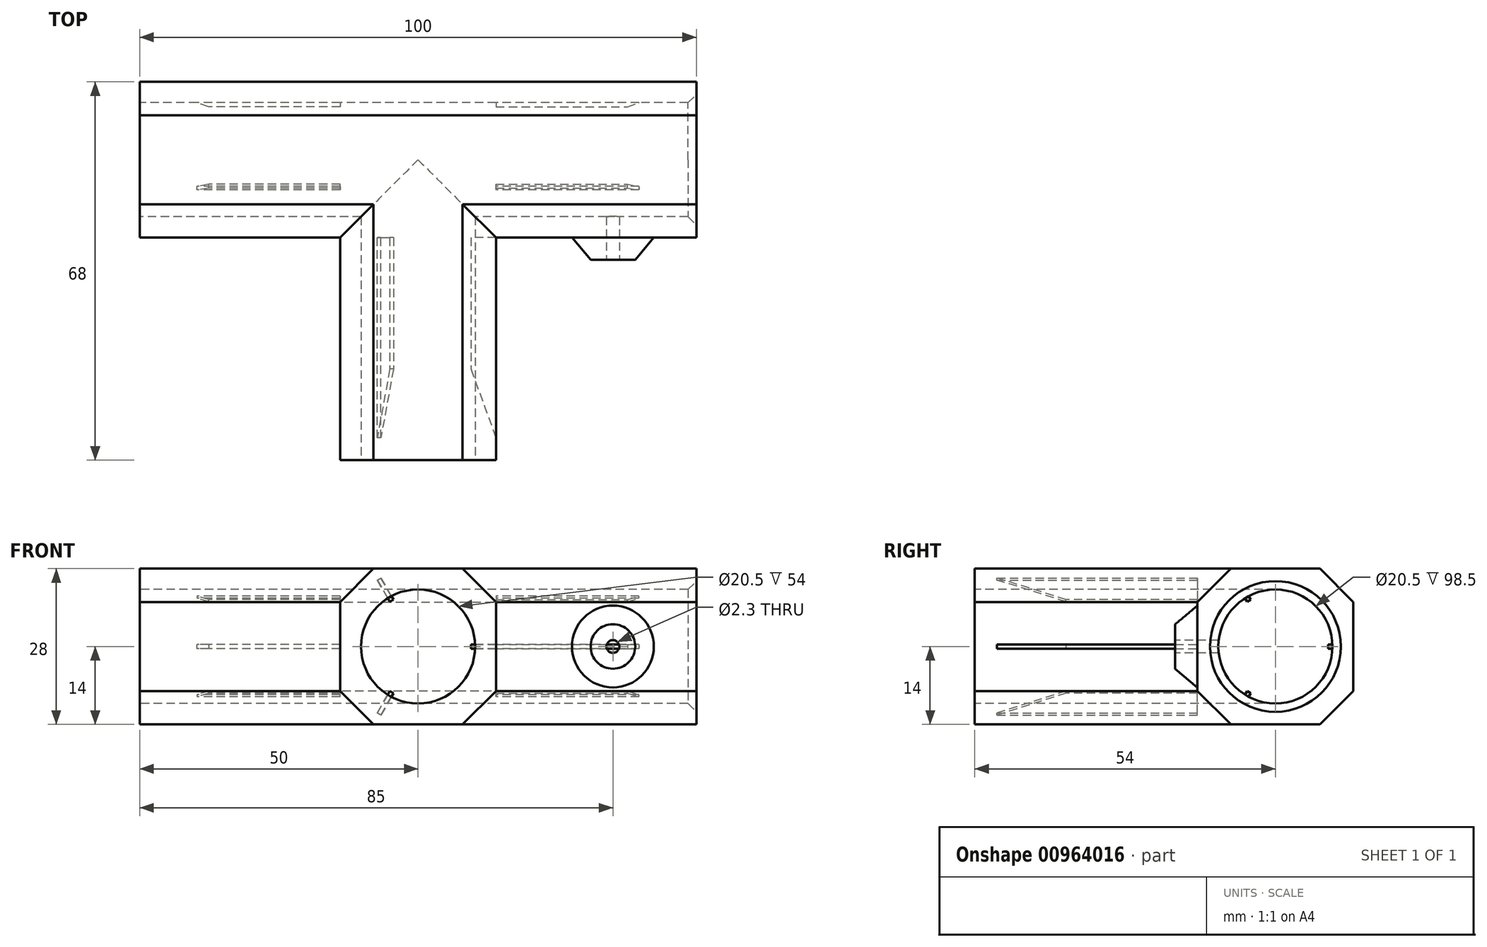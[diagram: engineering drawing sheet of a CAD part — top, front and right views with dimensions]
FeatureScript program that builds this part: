
annotation { "Feature Type Name" : "Feature", "Feature Type Description" : "" }
export const myFeature = defineFeature(function(context is Context, id is Id, definition is map)
    precondition{}
    {
        {
            var Q0;
            Q0=qCreatedBy(makeId("Top.planeOp"),FACE);
            var sketch = newSketch(context, id + "F0", { "sketchPlane" : qUnion([Q0])});
            skCircle(sketch, "E0", {"center": v(0, 0) * mm, "radius": 50 * mm, "construction": true});
            skLineSegment(sketch, "E1", {"start": v(-50, 0) * mm, "end": v(50, 0) * mm, "construction": true});
            skLineSegment(sketch, "E2", {"start": v(0, 50) * mm, "end": v(0, -50) * mm, "construction": true});
            skSolve(sketch);
        }
        {
            var Q0;
            Q0=qCreatedBy(makeId("Top.planeOp"),FACE);
            var sketch = newSketch(context, id + "F1", { "sketchPlane" : qUnion([Q0])});
            skLineSegment(sketch, "E3.bottom", {"start": v(-50, 14) * mm, "end": v(50, 14) * mm});
            skLineSegment(sketch, "E3.top", {"start": v(-50, -14) * mm, "end": v(-14, -14) * mm});
            skLineSegment(sketch, "E3.left", {"start": v(-50, 14) * mm, "end": v(-50, -14) * mm});
            skLineSegment(sketch, "E3.right", {"start": v(50, 14) * mm, "end": v(50, -14) * mm});
            skLineSegment(sketch, "E4.bottom", {"start": v(14, -54) * mm, "end": v(-14, -54) * mm});
            skLineSegment(sketch, "E4.left", {"start": v(14, -54) * mm, "end": v(14, -14) * mm});
            skLineSegment(sketch, "E4.right", {"start": v(-14, -54) * mm, "end": v(-14, -14) * mm});
            skLineSegment(sketch, "E5.trimOffspring", {"start": v(14, -14) * mm, "end": v(50, -14) * mm});
            skLineSegment(sketch, "E6", {"start": v(35, 0) * mm, "end": v(35, -18) * mm, "construction": true});
            skLineSegment(sketch, "E7", {"start": v(42.36, -14) * mm, "end": v(39, -18) * mm});
            skLineSegment(sketch, "E8", {"start": v(39, -18) * mm, "end": v(31, -18) * mm});
            skLineSegment(sketch, "E9.MirrorCS", {"start": v(27.64, -14) * mm, "end": v(31, -18) * mm});
            skLineSegment(sketch, "E10", {"start": v(35, -18) * mm, "end": v(35, -14) * mm});
            skSolve(sketch);
        }
        {
            var Q0;
            Q0=makeQuery(id+"F1.imprint","IMPRINT",FACE,{"disambiguationData":[TD([[makeQuery(id+"F1.imprint","IMPRINT",EDGE,{"derivedFrom":sQuery(id+"F1.wireOp",EDGE,"E3.bottom")}),-1.0]])]});
            extrude(context, id + "F2", {"entities" : qUnion([Q0]), "depth" : 28 * mm, "offsetDistance" : 25 * mm, "symmetric" : true});
        }
        {
            var Q0;
            Q0=makeQuery(id+"F2.opExtrude","SWEPT_FACE",FACE,{"disambiguationData":[OSD([sQuery(id+"F1.wireOp",EDGE,"E3.left")])]});
            var sketch = newSketch(context, id + "F3", { "sketchPlane" : qUnion([Q0])});
            skCircle(sketch, "E11", {"center": v(0, 0) * mm, "radius": 10.25 * mm});
            skSolve(sketch);
        }
        {
            var Q0;
            Q0 = qSketchRegion(id + "F3", true);
            extrude(context, id + "F4", {"entities" : qUnion([Q0]), "operationType" : NewBodyOperationType.REMOVE, "endBound" : BoundingType.THROUGH_ALL, "oppositeDirection" : true, "depth" : 25 * mm, "offsetDistance" : 25 * mm});
        }
        {
            var Q0;
            Q0=makeQuery(id+"F2.opExtrude","SWEPT_FACE",FACE,{"disambiguationData":[OSD([sQuery(id+"F1.wireOp",EDGE,"E4.bottom")])]});
            var sketch = newSketch(context, id + "F5", { "sketchPlane" : qUnion([Q0])});
            skCircle(sketch, "E12", {"center": v(0, 0) * mm, "radius": 10.25 * mm});
            skSolve(sketch);
        }
        {
            var Q0;
            Q0 = qSketchRegion(id + "F5", true);
            extrude(context, id + "F6", {"entities" : qUnion([Q0]), "operationType" : NewBodyOperationType.REMOVE, "endBound" : BoundingType.UP_TO_NEXT, "oppositeDirection" : true, "depth" : 25 * mm, "offsetDistance" : 25 * mm});
        }
        {
            var Q0;
            {var subQ0=sQuery(id+"F1.wireOp",EDGE,"E7");Q0=makeQuery(id+"F1.imprint","IMPRINT",FACE,{"disambiguationData":[TD([[makeQuery(id+"F1.imprint","IMPRINT",EDGE,{"derivedFrom":subQ0}),-1.0]])]});}
            var Q1;
            Q1=sQuery(id+"F1.wireOp",EDGE,"E10");
            revolve(context, id + "F7", {"operationType" : NewBodyOperationType.ADD, "surfaceOperationType" : NewSurfaceOperationType.NEW, "entities" : qUnion([Q0]), "axis" : qUnion([Q1]), "revolveType" : RevolveType.FULL});
        }
        {
            var Q0;
            Q0=makeQuery(id+"F7.opRevolve","SWEPT_FACE",FACE,{"disambiguationData":[OSD([sQuery(id+"F1.wireOp",EDGE,"E8")])]});
            var sketch = newSketch(context, id + "F8", { "sketchPlane" : qUnion([Q0])});
            skCircle(sketch, "E13", {"center": v(35, 0) * mm, "radius": 1.15 * mm});
            skSolve(sketch);
        }
        {
            var Q0;
            Q0 = qSketchRegion(id + "F8", true);
            extrude(context, id + "F9", {"entities" : qUnion([Q0]), "operationType" : NewBodyOperationType.REMOVE, "endBound" : BoundingType.UP_TO_NEXT, "oppositeDirection" : true, "depth" : 25 * mm, "offsetDistance" : 25 * mm});
        }
        {
            var Q0;
            Q0=makeQuery(id+"F2.opExtrude","CAP_EDGE",EDGE,{"disambiguationData":[OSD([sQuery(id+"F1.wireOp",EDGE,"E3.bottom")])],"isStart":true});
            var Q1;
            Q1=makeQuery(id+"F2.opExtrude","CAP_EDGE",EDGE,{"disambiguationData":[OSD([sQuery(id+"F1.wireOp",EDGE,"E3.bottom")])],"isStart":false});
            var Q2;
            Q2=makeQuery(id+"F2.opExtrude","CAP_EDGE",EDGE,{"disambiguationData":[OSD([sQuery(id+"F1.wireOp",EDGE,"E3.top")])],"isStart":true});
            var Q3;
            Q3=makeQuery(id+"F2.opExtrude","CAP_EDGE",EDGE,{"disambiguationData":[OSD([sQuery(id+"F1.wireOp",EDGE,"E5.trimOffspring")])],"isStart":true});
            var Q4;
            Q4=makeQuery(id+"F2.opExtrude","CAP_EDGE",EDGE,{"disambiguationData":[OSD([sQuery(id+"F1.wireOp",EDGE,"E4.left")])],"isStart":true});
            var Q5;
            Q5=makeQuery(id+"F2.opExtrude","CAP_EDGE",EDGE,{"disambiguationData":[OSD([sQuery(id+"F1.wireOp",EDGE,"E4.right")])],"isStart":true});
            var Q6;
            Q6=makeQuery(id+"F2.opExtrude","CAP_EDGE",EDGE,{"disambiguationData":[OSD([sQuery(id+"F1.wireOp",EDGE,"E4.right")])],"isStart":false});
            var Q7;
            Q7=makeQuery(id+"F2.opExtrude","CAP_EDGE",EDGE,{"disambiguationData":[OSD([sQuery(id+"F1.wireOp",EDGE,"E3.top")])],"isStart":false});
            var Q8;
            Q8=makeQuery(id+"F2.opExtrude","CAP_EDGE",EDGE,{"disambiguationData":[OSD([sQuery(id+"F1.wireOp",EDGE,"E5.trimOffspring")])],"isStart":false});
            var Q9;
            Q9=makeQuery(id+"F2.opExtrude","CAP_EDGE",EDGE,{"disambiguationData":[OSD([sQuery(id+"F1.wireOp",EDGE,"E4.left")])],"isStart":false});
            chamfer(context, id + "F10", {"entities" : qUnion([Q0, Q1, Q2, Q3, Q4, Q5, Q6, Q7, Q8, Q9]), "width" : 6 * mm, "tangentPropagation" : true});
        }
        {
            var Q0;
            Q0=makeQuery(id+"F4.boolean.opBoolean","COPY",EDGE,{"derivedFrom":makeQuery(id+"F4.opExtrude","CAP_EDGE",EDGE,{"disambiguationData":[OSD([sQuery(id+"F3.wireOp",EDGE,"E11")])],"isStart":true})});
            var Q1;
            Q1=makeQuery(id+"F6.boolean.opBoolean","COPY",EDGE,{"derivedFrom":makeQuery(id+"F6.opExtrude","CAP_EDGE",EDGE,{"disambiguationData":[OSD([sQuery(id+"F5.wireOp",EDGE,"E12")])],"isStart":true})});
            var Q2;
            Q2=makeQuery(id+"F4.boolean.opBoolean","INTERSECT",EDGE,{"derivedFrom":[makeQuery(id+"F2.opExtrude","SWEPT_FACE",FACE,{"disambiguationData":[OSD([sQuery(id+"F1.wireOp",EDGE,"E3.right")])]}),makeQuery(id+"F4.opExtrude","SWEPT_FACE",FACE,{"disambiguationData":[OSD([sQuery(id+"F3.wireOp",EDGE,"E11")])]})]});
            chamfer(context, id + "F11", {"entities" : qUnion([Q0, Q1, Q2]), "width" : 1.5 * mm, "tangentPropagation" : true});
        }
        {
            var Q0;
            Q0=qCreatedBy(makeId("Top.planeOp"),FACE);
            var sketch = newSketch(context, id + "F12", { "sketchPlane" : qUnion([Q0])});
            skLineSegment(sketch, "E14", {"start": v(0, 0) * mm, "end": v(50, 0) * mm, "construction": true});
            skLineSegment(sketch, "E15", {"start": v(14, 14) * mm, "end": v(14, 9.5) * mm});
            skLineSegment(sketch, "E16", {"start": v(14, 9.5) * mm, "end": v(37.64, 9.5) * mm});
            skLineSegment(sketch, "E17", {"start": v(37.64, 9.5) * mm, "end": v(50, 14) * mm});
            skLineSegment(sketch, "E18", {"start": v(50, 14) * mm, "end": v(14, 14) * mm});
            skSolve(sketch);
        }
        {
            var Q0;
            Q0 = qSketchRegion(id + "F12", true);
            extrude(context, id + "F13", {"entities" : qUnion([Q0]), "depth" : 0.75 * mm, "offsetDistance" : 25 * mm, "symmetric" : true});
        }
        {
            var Q0;
            Q0=makeQuery(id+"F13.opExtrude","SWEPT_BODY",BODY,{"disambiguationData":[OSD([sQuery(id+"F12.wireOp",EDGE,"E15"),sQuery(id+"F12.wireOp",EDGE,"E16"),sQuery(id+"F12.wireOp",EDGE,"E17"),sQuery(id+"F12.wireOp",EDGE,"E18")])]});
            var Q1;
            Q1=sQuery(id+"F0.wireOp",EDGE,"E1");
            circularPattern(context, id + "F14", {"entities" : qUnion([Q0]), "axis" : qUnion([Q1]), "angle" : 360 * degree, "instanceCount" : 3, "equalSpace" : true});
        }
        {
            var Q0;
            Q0=makeQuery(id+"F14.opPattern","COPY",BODY,{"derivedFrom":makeQuery(id+"F13.opExtrude","SWEPT_BODY",BODY,{"disambiguationData":[OSD([sQuery(id+"F12.wireOp",EDGE,"E15"),sQuery(id+"F12.wireOp",EDGE,"E16"),sQuery(id+"F12.wireOp",EDGE,"E17"),sQuery(id+"F12.wireOp",EDGE,"E18")])]}),"instanceName":"1"});
            var Q1;
            Q1=makeQuery(id+"F14.opPattern","COPY",BODY,{"derivedFrom":makeQuery(id+"F13.opExtrude","SWEPT_BODY",BODY,{"disambiguationData":[OSD([sQuery(id+"F12.wireOp",EDGE,"E15"),sQuery(id+"F12.wireOp",EDGE,"E16"),sQuery(id+"F12.wireOp",EDGE,"E17"),sQuery(id+"F12.wireOp",EDGE,"E18")])]}),"instanceName":"2"});
            var Q2;
            Q2=makeQuery(id+"F14.opPattern","COPY",BODY,{"derivedFrom":makeQuery(id+"F13.opExtrude","SWEPT_BODY",BODY,{"disambiguationData":[OSD([sQuery(id+"F12.wireOp",EDGE,"E15"),sQuery(id+"F12.wireOp",EDGE,"E16"),sQuery(id+"F12.wireOp",EDGE,"E17"),sQuery(id+"F12.wireOp",EDGE,"E18")])]}),"instanceName":"3"});
            var Q3;
            Q3=makeQuery(id+"F14.opPattern","COPY",BODY,{"derivedFrom":makeQuery(id+"F13.opExtrude","SWEPT_BODY",BODY,{"disambiguationData":[OSD([sQuery(id+"F12.wireOp",EDGE,"E15"),sQuery(id+"F12.wireOp",EDGE,"E16"),sQuery(id+"F12.wireOp",EDGE,"E17"),sQuery(id+"F12.wireOp",EDGE,"E18")])]}),"instanceName":"4"});
            var Q4;
            Q4=makeQuery(id+"F13.opExtrude","SWEPT_BODY",BODY,{"disambiguationData":[OSD([sQuery(id+"F12.wireOp",EDGE,"E15"),sQuery(id+"F12.wireOp",EDGE,"E16"),sQuery(id+"F12.wireOp",EDGE,"E17"),sQuery(id+"F12.wireOp",EDGE,"E18")])]});
            var Q5;
            Q5=sQuery(id+"F0.wireOp",EDGE,"E0");
            circularPattern(context, id + "F15", {"entities" : qUnion([Q0, Q1, Q2, Q3, Q4]), "axis" : qUnion([Q5]), "angle" : 90 * degree, "instanceCount" : 2, "oppositeDirection" : true, "equalSpace" : true});
        }
        {
            var Q0;
            Q0=makeQuery(id+"F13.opExtrude","SWEPT_BODY",BODY,{"disambiguationData":[OSD([sQuery(id+"F12.wireOp",EDGE,"E15"),sQuery(id+"F12.wireOp",EDGE,"E16"),sQuery(id+"F12.wireOp",EDGE,"E17"),sQuery(id+"F12.wireOp",EDGE,"E18")])]});
            var Q1;
            Q1=makeQuery(id+"F14.opPattern","COPY",BODY,{"derivedFrom":makeQuery(id+"F13.opExtrude","SWEPT_BODY",BODY,{"disambiguationData":[OSD([sQuery(id+"F12.wireOp",EDGE,"E15"),sQuery(id+"F12.wireOp",EDGE,"E16"),sQuery(id+"F12.wireOp",EDGE,"E17"),sQuery(id+"F12.wireOp",EDGE,"E18")])]}),"instanceName":"4"});
            var Q2;
            Q2=makeQuery(id+"F14.opPattern","COPY",BODY,{"derivedFrom":makeQuery(id+"F13.opExtrude","SWEPT_BODY",BODY,{"disambiguationData":[OSD([sQuery(id+"F12.wireOp",EDGE,"E15"),sQuery(id+"F12.wireOp",EDGE,"E16"),sQuery(id+"F12.wireOp",EDGE,"E17"),sQuery(id+"F12.wireOp",EDGE,"E18")])]}),"instanceName":"3"});
            var Q3;
            Q3=makeQuery(id+"F14.opPattern","COPY",BODY,{"derivedFrom":makeQuery(id+"F13.opExtrude","SWEPT_BODY",BODY,{"disambiguationData":[OSD([sQuery(id+"F12.wireOp",EDGE,"E15"),sQuery(id+"F12.wireOp",EDGE,"E16"),sQuery(id+"F12.wireOp",EDGE,"E17"),sQuery(id+"F12.wireOp",EDGE,"E18")])]}),"instanceName":"2"});
            var Q4;
            Q4=makeQuery(id+"F14.opPattern","COPY",BODY,{"derivedFrom":makeQuery(id+"F13.opExtrude","SWEPT_BODY",BODY,{"disambiguationData":[OSD([sQuery(id+"F12.wireOp",EDGE,"E15"),sQuery(id+"F12.wireOp",EDGE,"E16"),sQuery(id+"F12.wireOp",EDGE,"E17"),sQuery(id+"F12.wireOp",EDGE,"E18")])]}),"instanceName":"1"});
            var Q5;
            Q5=qCreatedBy(makeId("Right.planeOp"),FACE);
            mirror(context, id + "F16", {"operationType" : NewBodyOperationType.ADD, "entities" : qUnion([Q0, Q1, Q2, Q3, Q4]), "mirrorPlane" : qUnion([Q5])});
        }
    });
